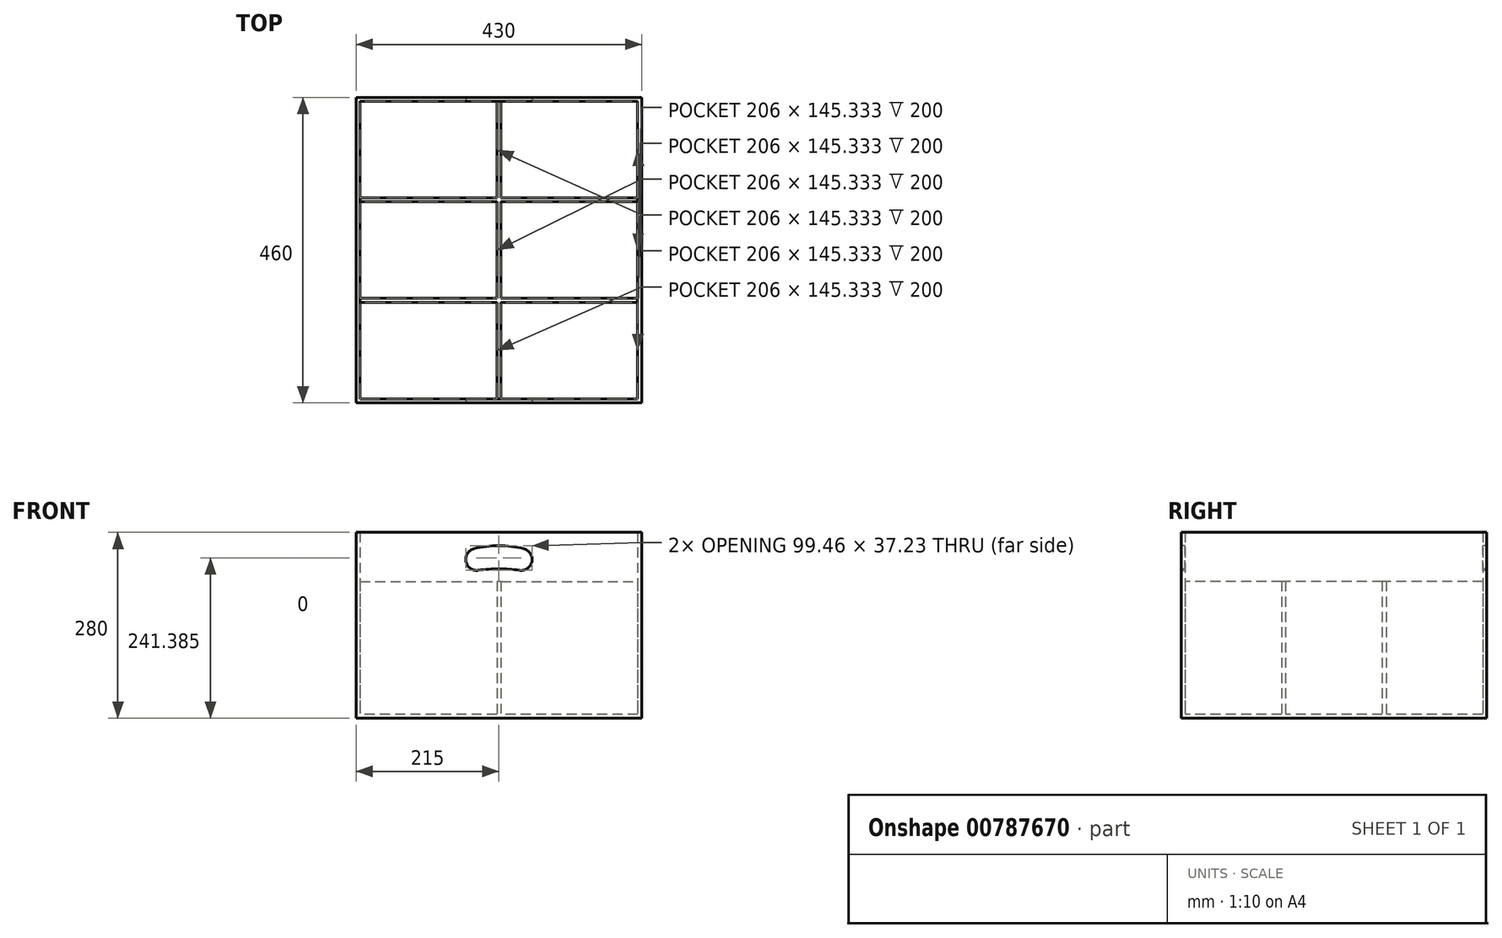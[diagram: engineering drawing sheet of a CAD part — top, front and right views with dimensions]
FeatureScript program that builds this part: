
annotation { "Feature Type Name" : "Feature", "Feature Type Description" : "" }
export const myFeature = defineFeature(function(context is Context, id is Id, definition is map)
    precondition{}
    {
        {
            var Q0;
            Q0=qCreatedBy(makeId("Top.planeOp"),FACE);
            var sketch = newSketch(context, id + "F0", { "sketchPlane" : qUnion([Q0])});
            skLineSegment(sketch, "E0.bottom", {"start": v(215, 230) * mm, "end": v(-215, 230) * mm});
            skLineSegment(sketch, "E0.top", {"start": v(215, -230) * mm, "end": v(-215, -230) * mm});
            skLineSegment(sketch, "E0.left", {"start": v(215, 230) * mm, "end": v(215, -230) * mm});
            skLineSegment(sketch, "E0.right", {"start": v(-215, 230) * mm, "end": v(-215, -230) * mm});
            skPoint(sketch, "E0.middle", {"position": v(0, 0) * mm});
            skSolve(sketch);
        }
        {
            var Q0;
            Q0 = qSketchRegion(id + "F0", true);
            extrude(context, id + "F1", {"entities" : qUnion([Q0]), "depth" : 280 * mm, "offsetDistance" : 25 * mm});
        }
        {
            var Q0;
            Q0=makeQuery(id+"F1.opExtrude","CAP_FACE",FACE,{"disambiguationData":[OSD([sQuery(id+"F0.wireOp",EDGE,"E0.bottom"),sQuery(id+"F0.wireOp",EDGE,"E0.top"),sQuery(id+"F0.wireOp",EDGE,"E0.left"),sQuery(id+"F0.wireOp",EDGE,"E0.right")])],"isStart":false});
            shell(context, id + "F2", {"entities" : qUnion([Q0]), "thickness" : 6 * mm});
        }
        {
            var Q0;
            Q0=makeQuery(id+"F1.opExtrude","SWEPT_FACE",FACE,{"disambiguationData":[OSD([sQuery(id+"F0.wireOp",EDGE,"E0.top")])]});
            var sketch = newSketch(context, id + "F3", { "sketchPlane" : qUnion([Q0])});
            skArc(sketch, "E1", {"start": v(37.58, 255.22) * mm, "mid": v(0, 260) * mm, "end": v(-37.58, 255.22) * mm});
            skArc(sketch, "E2", {"start": v(31.06, 222.77) * mm, "mid": v(0, 225) * mm, "end": v(-31.06, 222.77) * mm});
            skArc(sketch, "E3", {"start": v(31.06, 222.77) * mm, "mid": v(49.68, 235.9) * mm, "end": v(37.58, 255.22) * mm});
            skArc(sketch, "E4", {"start": v(-37.58, 255.22) * mm, "mid": v(-49.68, 235.9) * mm, "end": v(-31.06, 222.77) * mm});
            skSolve(sketch);
        }
        {
            var Q0;
            Q0 = qSketchRegion(id + "F3", true);
            extrude(context, id + "F4", {"entities" : qUnion([Q0]), "operationType" : NewBodyOperationType.REMOVE, "endBound" : BoundingType.THROUGH_ALL, "oppositeDirection" : true, "depth" : 25 * mm, "offsetDistance" : 25 * mm});
        }
        {
            var Q0;
            Q0=makeQuery(id+"F2.opShell","OFFSET_FACE",FACE,{"disambiguationData":[OSD([sQuery(id+"F0.wireOp",EDGE,"E0.bottom"),sQuery(id+"F0.wireOp",EDGE,"E0.top"),sQuery(id+"F0.wireOp",EDGE,"E0.left"),sQuery(id+"F0.wireOp",EDGE,"E0.right")])]});
            var sketch = newSketch(context, id + "F5", { "sketchPlane" : qUnion([Q0])});
            skLineSegment(sketch, "E5.bottom", {"start": v(3, 224) * mm, "end": v(-3, 224) * mm});
            skLineSegment(sketch, "E5.top", {"start": v(3, -224) * mm, "end": v(-3, -224) * mm});
            skLineSegment(sketch, "E5.left", {"start": v(3, 224) * mm, "end": v(3, -224) * mm});
            skLineSegment(sketch, "E5.right", {"start": v(-3, 224) * mm, "end": v(-3, -224) * mm});
            skPoint(sketch, "E5.middle", {"position": v(0, 0) * mm});
            skLineSegment(sketch, "E6.bottom", {"start": v(-209, 78.67) * mm, "end": v(-3, 78.67) * mm});
            skLineSegment(sketch, "E6.top", {"start": v(-209, 72.67) * mm, "end": v(-3, 72.67) * mm});
            skLineSegment(sketch, "E6.left", {"start": v(-209, 78.67) * mm, "end": v(-209, 72.67) * mm});
            skLineSegment(sketch, "E6.right", {"start": v(-3, 78.67) * mm, "end": v(-3, 72.67) * mm});
            skLineSegment(sketch, "E7.bottom", {"start": v(-209, -72.67) * mm, "end": v(-3, -72.67) * mm});
            skLineSegment(sketch, "E7.top", {"start": v(-209, -78.67) * mm, "end": v(-3, -78.67) * mm});
            skLineSegment(sketch, "E7.left", {"start": v(-209, -72.67) * mm, "end": v(-209, -78.67) * mm});
            skLineSegment(sketch, "E7.right", {"start": v(-3, -72.67) * mm, "end": v(-3, -78.67) * mm});
            skLineSegment(sketch, "E8.bottom", {"start": v(3, -78.67) * mm, "end": v(209, -78.67) * mm});
            skLineSegment(sketch, "E8.top", {"start": v(3, -72.67) * mm, "end": v(209, -72.67) * mm});
            skLineSegment(sketch, "E8.left", {"start": v(3, -78.67) * mm, "end": v(3, -72.67) * mm});
            skLineSegment(sketch, "E8.right", {"start": v(209, -78.67) * mm, "end": v(209, -72.67) * mm});
            skLineSegment(sketch, "E9.bottom", {"start": v(3, 78.67) * mm, "end": v(209, 78.67) * mm});
            skLineSegment(sketch, "E9.top", {"start": v(3, 72.67) * mm, "end": v(209, 72.67) * mm});
            skLineSegment(sketch, "E9.left", {"start": v(3, 78.67) * mm, "end": v(3, 72.67) * mm});
            skLineSegment(sketch, "E9.right", {"start": v(209, 78.67) * mm, "end": v(209, 72.67) * mm});
            skLineSegment(sketch, "E10", {"start": v(-106, 78.67) * mm, "end": v(-106, 224) * mm, "construction": true});
            skLineSegment(sketch, "E11", {"start": v(-106, 72.67) * mm, "end": v(-106, -72.67) * mm, "construction": true});
            skLineSegment(sketch, "E12", {"start": v(-106, -78.67) * mm, "end": v(-106, -224) * mm, "construction": true});
            skSolve(sketch);
        }
        {
            var Q0;
            Q0 = qSketchRegion(id + "F5", true);
            extrude(context, id + "F6", {"entities" : qUnion([Q0]), "operationType" : NewBodyOperationType.ADD, "depth" : 200 * mm, "offsetDistance" : 25 * mm});
        }
    });
